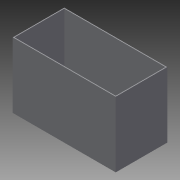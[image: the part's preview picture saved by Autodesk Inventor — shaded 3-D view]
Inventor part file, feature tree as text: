
AUTODESK INVENTOR PART (.ipt)
format: ipt  version: 2013 (Build 170138000, 138)  size: 78,848 bytes
history: native  units: in
note: dims shown in document units (in); Inventor stores cm internally (conversion verified against a paired STEP export)
features: extrude x2, sketch x2
ambient origin geometry x8: Origin, YZ Plane, XZ Plane, XY Plane, X Axis, Y Axis, Z Axis, Center Point
bodies: Solid1 (feature_tree)
feature tree (4):
  extrude  "Extrusion1"  Depth=5.5in
  extrude  "Extrusion2"  Depth=0.0938in
  sketch  "Sketch1"  dims[d0=11.0in d1=5.5in]
  sketch  "Sketch2"  dims[d2=7.0in d3=0.0in d4=0.0938in d5=6.9062in d6=0.0in]
